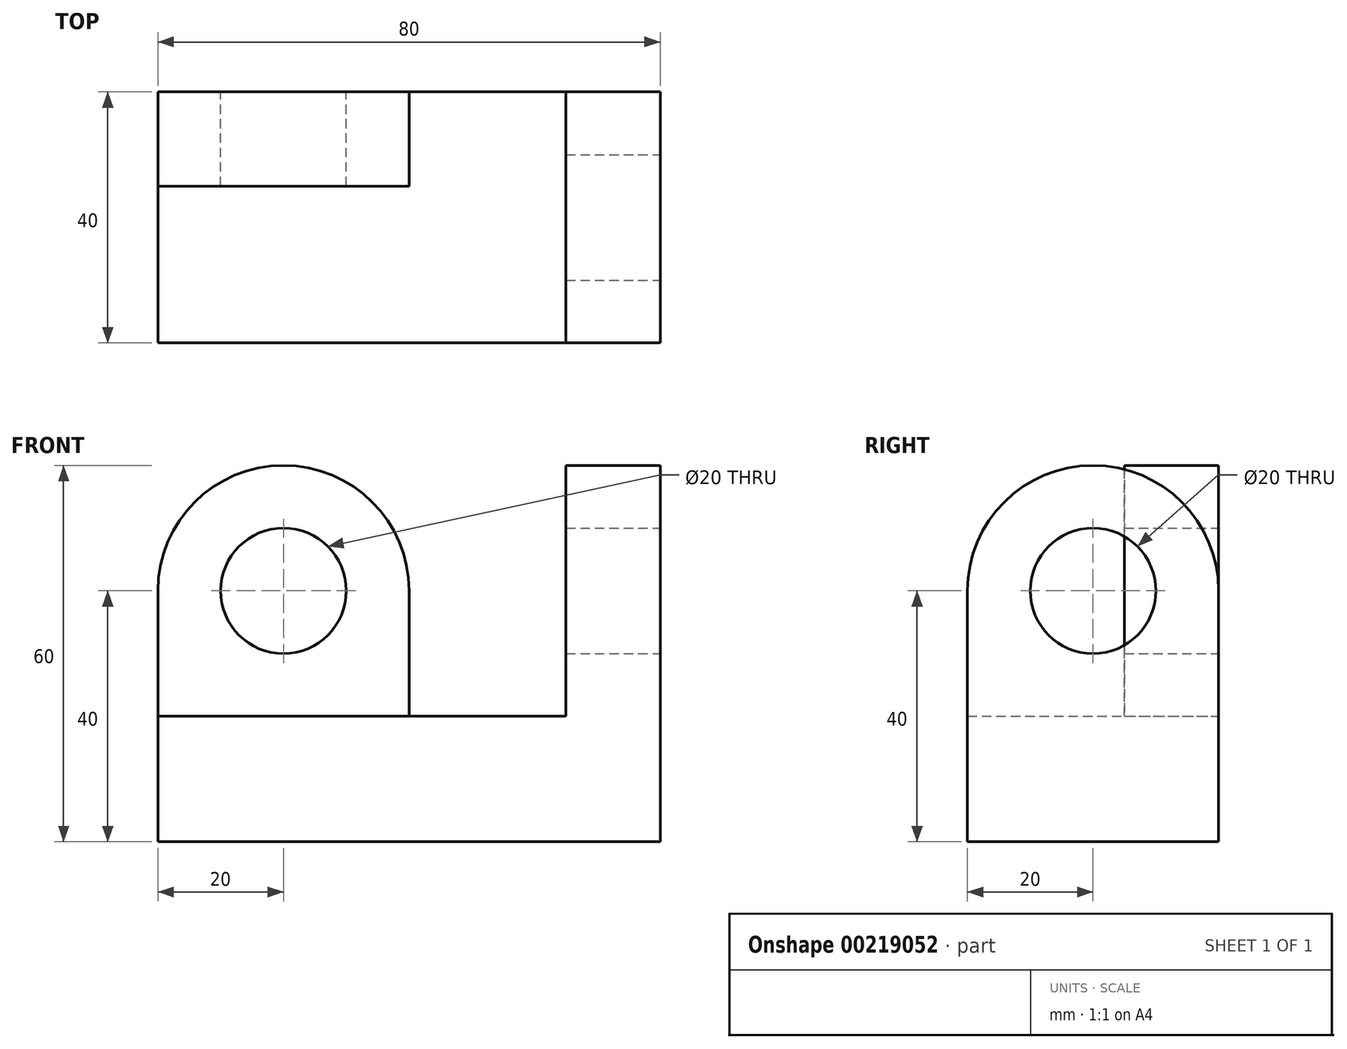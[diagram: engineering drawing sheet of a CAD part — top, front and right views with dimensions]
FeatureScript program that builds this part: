
annotation { "Feature Type Name" : "Feature", "Feature Type Description" : "" }
export const myFeature = defineFeature(function(context is Context, id is Id, definition is map)
    precondition{}
    {
        {
            var Q0;
            Q0=qCreatedBy(makeId("Front.planeOp"),FACE);
            var sketch = newSketch(context, id + "F0", { "sketchPlane" : qUnion([Q0])});
            skLineSegment(sketch, "E0", {"start": v(0, 0) * mm, "end": v(80, 0) * mm});
            skLineSegment(sketch, "E1", {"start": v(80, 0) * mm, "end": v(80, 60) * mm});
            skLineSegment(sketch, "E2", {"start": v(80, 60) * mm, "end": v(65, 60) * mm});
            skLineSegment(sketch, "E3", {"start": v(65, 60) * mm, "end": v(65, 20) * mm});
            skLineSegment(sketch, "E4", {"start": v(65, 20) * mm, "end": v(0, 20) * mm});
            skLineSegment(sketch, "E5", {"start": v(0, 20) * mm, "end": v(0, 0) * mm});
            skLineSegment(sketch, "E6", {"start": v(0, 20) * mm, "end": v(0, 40) * mm});
            skCircle(sketch, "E7", {"center": v(20, 40) * mm, "radius": 10 * mm});
            skArc(sketch, "E8", {"start": v(40, 40) * mm, "mid": v(20, 60) * mm, "end": v(0, 40) * mm});
            skLineSegment(sketch, "E9", {"start": v(40, 40) * mm, "end": v(40, 20) * mm});
            skSolve(sketch);
        }
        {
            var Q0;
            Q0=makeQuery(id+"F0.imprint","IMPRINT",FACE,{"disambiguationData":[TD([[makeQuery(id+"F0.imprint","IMPRINT",EDGE,{"derivedFrom":sQuery(id+"F0.wireOp",EDGE,"E0")}),1.0]])]});
            extrude(context, id + "F1", {"entities" : qUnion([Q0]), "depth" : 40 * mm});
        }
        {
            var Q0;
            {var subQ0=sQuery(id+"F0.wireOp",EDGE,"E6");Q0=makeQuery(id+"F0.imprint","IMPRINT",FACE,{"disambiguationData":[TD([[makeQuery(id+"F0.imprint","IMPRINT",EDGE,{"derivedFrom":subQ0}),-1.0]])]});}
            extrude(context, id + "F2", {"entities" : qUnion([Q0]), "operationType" : NewBodyOperationType.ADD, "depth" : 15 * mm});
        }
        {
            var Q0;
            Q0=makeQuery(id+"F1.opExtrude","CAP_EDGE",EDGE,{"disambiguationData":[OSD([sQuery(id+"F0.wireOp",EDGE,"E2")])],"isStart":false});
            var Q1;
            Q1=makeQuery(id+"F1.opExtrude","CAP_EDGE",EDGE,{"disambiguationData":[OSD([sQuery(id+"F0.wireOp",EDGE,"E2")])],"isStart":true});
            fillet(context, id + "F3", {"entities" : qUnion([Q0, Q1]), "radius" : 20 * mm, "tangentPropagation" : true, "allowEdgeOverflow" : false});
        }
        {
            var Q0;
            Q0=makeQuery(id+"F1.opExtrude","SWEPT_FACE",FACE,{"disambiguationData":[OSD([sQuery(id+"F0.wireOp",EDGE,"E1")])]});
            var sketch = newSketch(context, id + "F4", { "sketchPlane" : qUnion([Q0])});
            skCircle(sketch, "E10", {"center": v(-20, 40) * mm, "radius": 10 * mm});
            skSolve(sketch);
        }
        {
            var Q0;
            Q0 = qSketchRegion(id + "F4", true);
            extrude(context, id + "F5", {"entities" : qUnion([Q0]), "operationType" : NewBodyOperationType.REMOVE, "endBound" : BoundingType.UP_TO_NEXT, "oppositeDirection" : true, "depth" : 25 * mm});
        }
    });
